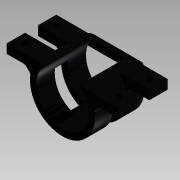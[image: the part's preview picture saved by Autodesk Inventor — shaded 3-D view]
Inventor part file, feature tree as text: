
AUTODESK INVENTOR PART (.ipt)
format: ipt  version: 2015 SP1 (Build 190203100, 203)  size: 285,184 bytes
history: native  units: mm
features: extrude x9, sketch x9, mirror x1, fillet x1, projected_geometry x1
ambient origin geometry x8: Origin, YZ Plane, XZ Plane, XY Plane, X Axis, Y Axis, Z Axis, Center Point
bodies: Solid1 (feature_tree)
feature tree (21):
  extrude  "Extrusion1"  TaperAngle=45.0deg  [1 undecoded]
  extrude  "Extrusion2"  Depth=25.4mm
  extrude  "Extrusion3"  Depth=10.0mm
  mirror  "Mirror2"
  extrude  "Extrusion7"  Depth=5.0mm
  extrude  "Extrusion8"  Depth=12.700083mm
  fillet  "Fillet1"  Radius=10.0mm
  extrude  "Extrusion9"  Depth=5.0mm
  extrude  "Extrusion10"  Depth=5.0mm
  extrude  "Extrusion11"  Depth=3.5mm
  extrude  "Extrusion12"  Depth=10.0mm TaperAngle=0.0deg
  sketch  "Sketch1"  dims[d9=135.0deg d10=45.0deg]
  sketch  "Sketch2"  dims[d21=2.0mm d22=25.4mm]
  sketch  "Sketch3"  dims[d23=10.0mm d24=0.0mm d25=3.5mm]
  sketch  "Sketch13"  dims[d26=3.5mm d27=5.0mm]
  sketch  "Sketch14"  dims[d28=5.0mm d30=12.700083mm d31=10.0mm d32=0.0mm]
  sketch  "Sketch15"  dims[d39=3.5mm d40=0.0mm d55=5.0mm]
  sketch  "Sketch18"  dims[d60=5.0mm d61=5.0mm]
  sketch  "Sketch19"  dims[d62=3.5mm d63=3.5mm]
  projected_geometry  "Projected Loop8"
  sketch  "Sketch20"  dims[d64=5.0mm d65=3.0mm d66=0.0mm d67=3.0mm d68=0.0mm d69=2.0mm d71=1.5mm d72=27.0mm d73=0.0mm d74=27.0mm d75=0.0mm d76=200.0mm d77=0.0mm d78=10.0mm d79=0.0mm]
note: 1 required parameter value undecoded (feature->parameter linkage not recoverable at this tier; creation-order binding heuristic only, values carry confidence <= 0.55)
